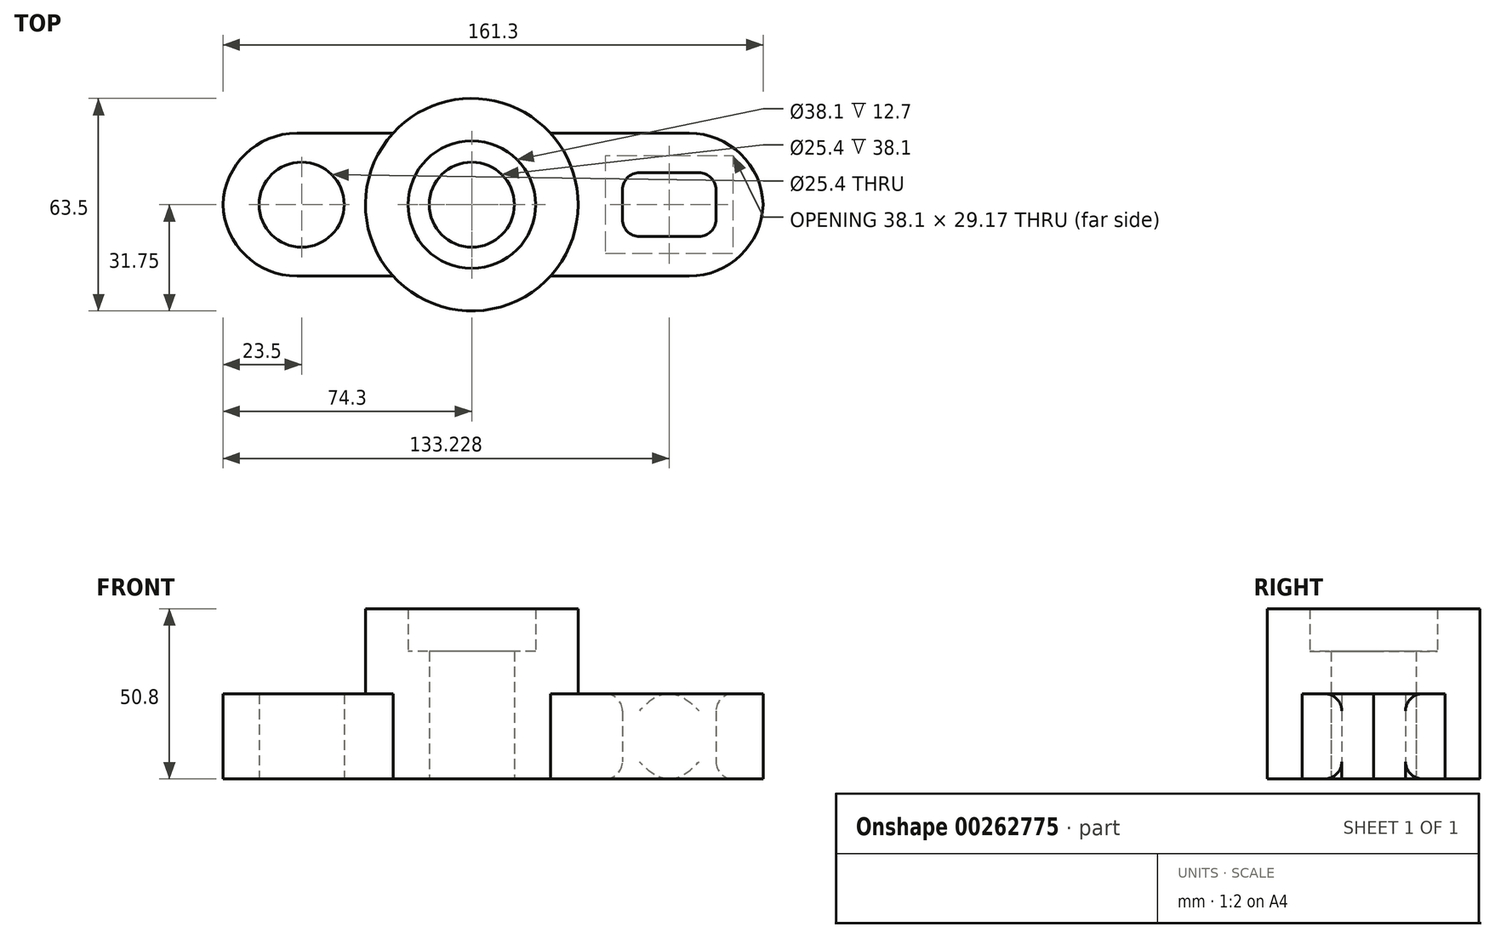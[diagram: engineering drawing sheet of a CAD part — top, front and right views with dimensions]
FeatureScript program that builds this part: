
annotation { "Feature Type Name" : "Feature", "Feature Type Description" : "" }
export const myFeature = defineFeature(function(context is Context, id is Id, definition is map)
    precondition{}
    {
        {
            var Q0;
            Q0=qCreatedBy(makeId("Top.planeOp"),FACE);
            var sketch = newSketch(context, id + "F0", { "sketchPlane" : qUnion([Q0])});
            skCircle(sketch, "E0", {"center": v(0, 0) * mm, "radius": 19.05 * mm});
            skLineSegment(sketch, "E1", {"start": v(0, 0) * mm, "end": v(-50.8, 0) * mm});
            skCircle(sketch, "E2", {"center": v(-50.8, 0) * mm, "radius": 12.7 * mm});
            skLineSegment(sketch, "E3", {"start": v(-50.8, 0) * mm, "end": v(44.96, 0) * mm});
            skCircle(sketch, "E4", {"center": v(0, 0) * mm, "radius": 31.75 * mm});
            skLineSegment(sketch, "E5", {"start": v(0, 0) * mm, "end": v(58.93, 0) * mm});
            skLineSegment(sketch, "E6.bottom", {"start": v(72.9, 9.53) * mm, "end": v(44.96, 9.52) * mm});
            skLineSegment(sketch, "E6.top", {"start": v(72.9, -9.52) * mm, "end": v(44.96, -9.53) * mm});
            skLineSegment(sketch, "E6.left", {"start": v(72.9, 9.52) * mm, "end": v(72.9, -9.53) * mm});
            skLineSegment(sketch, "E6.right", {"start": v(44.96, 9.52) * mm, "end": v(44.96, -9.53) * mm});
            skPoint(sketch, "E6.middle", {"position": v(58.93, 0) * mm});
            skCircle(sketch, "E7", {"center": v(0, 0) * mm, "radius": 12.7 * mm});
            skCircle(sketch, "E8", {"center": v(0, 0) * mm, "radius": 6.35 * mm});
            skLineSegment(sketch, "E9", {"start": v(-23.5, 21.34) * mm, "end": v(-74.3, 21.34) * mm});
            skLineSegment(sketch, "E10", {"start": v(-23.5, -21.34) * mm, "end": v(-74.3, -21.34) * mm});
            skLineSegment(sketch, "E11", {"start": v(-74.3, 21.34) * mm, "end": v(-74.3, -21.34) * mm});
            skLineSegment(sketch, "E12", {"start": v(23.5, 21.34) * mm, "end": v(87, 21.34) * mm});
            skLineSegment(sketch, "E13", {"start": v(23.5, -21.34) * mm, "end": v(87, -21.34) * mm});
            skLineSegment(sketch, "E14", {"start": v(87, 21.34) * mm, "end": v(87, -21.34) * mm});
            skSolve(sketch);
        }
        {
            var Q0;
            {var subQ5=sQuery(id+"F0.wireOp",EDGE,"E3");var subQ7=sQuery(id+"F0.wireOp",EDGE,"E0");var subQ8=makeQuery(id+"F0.imprint","INTERSECT",VERTEX,{"derivedFrom":[subQ7,subQ5]});Q0=makeQuery(id+"F0.imprint","IMPRINT",FACE,{"disambiguationData":[TD([[makeQuery(id+"F0.imprint","IMPRINT",EDGE,{"disambiguationData":[TD([[subQ8,1.0]])],"derivedFrom":subQ7}),-1.0]])]});}
            var Q1;
            {var subQ3=sQuery(id+"F0.wireOp",EDGE,"E3");var subQ5=sQuery(id+"F0.wireOp",EDGE,"E0");var subQ6=makeQuery(id+"F0.imprint","INTERSECT",VERTEX,{"derivedFrom":[subQ5,subQ3]});Q1=makeQuery(id+"F0.imprint","IMPRINT",FACE,{"disambiguationData":[TD([[makeQuery(id+"F0.imprint","IMPRINT",EDGE,{"disambiguationData":[TD([[subQ6,-1.0]])],"derivedFrom":subQ5}),-1.0]])]});}
            extrude(context, id + "F1", {"entities" : qUnion([Q0, Q1]), "depth" : 50.8 * mm});
        }
        {
            var Q0;
            {var subQ0=sQuery(id+"F0.wireOp",EDGE,"E3");var subQ1=sQuery(id+"F0.wireOp",EDGE,"E0");var subQ2=makeQuery(id+"F0.imprint","INTERSECT",VERTEX,{"derivedFrom":[subQ1,subQ0]});Q0=makeQuery(id+"F0.imprint","IMPRINT",FACE,{"disambiguationData":[TD([[makeQuery(id+"F0.imprint","IMPRINT",EDGE,{"disambiguationData":[TD([[subQ2,1.0]])],"derivedFrom":subQ1}),1.0]])]});}
            var Q1;
            {var subQ0=sQuery(id+"F0.wireOp",EDGE,"E3");var subQ1=sQuery(id+"F0.wireOp",EDGE,"E0");var subQ2=makeQuery(id+"F0.imprint","INTERSECT",VERTEX,{"derivedFrom":[subQ1,subQ0]});Q1=makeQuery(id+"F0.imprint","IMPRINT",FACE,{"disambiguationData":[TD([[makeQuery(id+"F0.imprint","IMPRINT",EDGE,{"disambiguationData":[TD([[subQ2,-1.0]])],"derivedFrom":subQ1}),1.0]])]});}
            extrude(context, id + "F2", {"entities" : qUnion([Q0, Q1]), "operationType" : NewBodyOperationType.ADD, "depth" : 38.1 * mm});
        }
        {
            var Q0;
            {var subQ0=sQuery(id+"F0.wireOp",EDGE,"E7");var subQ1=sQuery(id+"F0.wireOp",EDGE,"E3");var subQ2=makeQuery(id+"F0.imprint","INTERSECT",VERTEX,{"derivedFrom":[subQ1,subQ0]});Q0=makeQuery(id+"F0.imprint","IMPRINT",FACE,{"disambiguationData":[TD([[makeQuery(id+"F0.imprint","IMPRINT",EDGE,{"disambiguationData":[TD([[subQ2,-1.0]])],"derivedFrom":subQ1}),1.0]])]});}
            var Q1;
            {var subQ0=sQuery(id+"F0.wireOp",EDGE,"E7");var subQ1=sQuery(id+"F0.wireOp",EDGE,"E3");var subQ2=makeQuery(id+"F0.imprint","INTERSECT",VERTEX,{"derivedFrom":[subQ1,subQ0]});Q1=makeQuery(id+"F0.imprint","IMPRINT",FACE,{"disambiguationData":[TD([[makeQuery(id+"F0.imprint","IMPRINT",EDGE,{"disambiguationData":[TD([[subQ2,-1.0]])],"derivedFrom":subQ1}),-1.0]])]});}
            extrude(context, id + "F3", {"entities" : qUnion([Q0, Q1]), "operationType" : NewBodyOperationType.ADD, "depth" : 25.4 * mm});
        }
        {
            var Q0;
            Q0=makeQuery(id+"F0.imprint","IMPRINT",FACE,{"disambiguationData":[TD([[makeQuery(id+"F0.imprint","IMPRINT",EDGE,{"derivedFrom":sQuery(id+"F0.wireOp",EDGE,"E2")}),-1.0]])]});
            var Q1;
            {var subQ4=sQuery(id+"F0.wireOp",EDGE,"E6.bottom");Q1=makeQuery(id+"F0.imprint","IMPRINT",FACE,{"disambiguationData":[TD([[makeQuery(id+"F0.imprint","IMPRINT",EDGE,{"derivedFrom":subQ4}),-1.0]])]});}
            extrude(context, id + "F4", {"entities" : qUnion([Q0, Q1]), "operationType" : NewBodyOperationType.ADD, "depth" : 25.4 * mm});
        }
        {
            var Q0;
            Q0=makeQuery(id+"F4.opExtrude","SWEPT_EDGE",EDGE,{"disambiguationData":[OSD([sQuery(id+"F0.wireOp",EDGE,"E12"),sQuery(id+"F0.wireOp",EDGE,"E14")])]});
            var Q1;
            Q1=makeQuery(id+"F4.opExtrude","SWEPT_EDGE",EDGE,{"disambiguationData":[OSD([sQuery(id+"F0.wireOp",EDGE,"E13"),sQuery(id+"F0.wireOp",EDGE,"E14")])]});
            var Q2;
            Q2=makeQuery(id+"F4.opExtrude","SWEPT_EDGE",EDGE,{"disambiguationData":[OSD([sQuery(id+"F0.wireOp",EDGE,"E9"),sQuery(id+"F0.wireOp",EDGE,"E11")])]});
            var Q3;
            Q3=makeQuery(id+"F4.opExtrude","SWEPT_EDGE",EDGE,{"disambiguationData":[OSD([sQuery(id+"F0.wireOp",EDGE,"E10"),sQuery(id+"F0.wireOp",EDGE,"E11")])]});
            fillet(context, id + "F5", {"entities" : qUnion([Q0, Q1, Q2, Q3]), "radius" : 22.08 * mm, "tangentPropagation" : true, "allowEdgeOverflow" : false});
        }
        {
            var Q0;
            Q0=makeQuery(id+"F4.opExtrude","SWEPT_FACE",FACE,{"disambiguationData":[OSD([sQuery(id+"F0.wireOp",EDGE,"E6.left")])]});
            fillet(context, id + "F6", {"entities" : qUnion([Q0]), "radius" : 5.08 * mm, "tangentPropagation" : true, "allowEdgeOverflow" : false});
        }
        {
            var Q0;
            Q0=makeQuery(id+"F4.opExtrude","SWEPT_FACE",FACE,{"disambiguationData":[OSD([sQuery(id+"F0.wireOp",EDGE,"E6.right")])]});
            fillet(context, id + "F7", {"entities" : qUnion([Q0]), "radius" : 5.08 * mm, "tangentPropagation" : true, "allowEdgeOverflow" : false});
        }
    });
